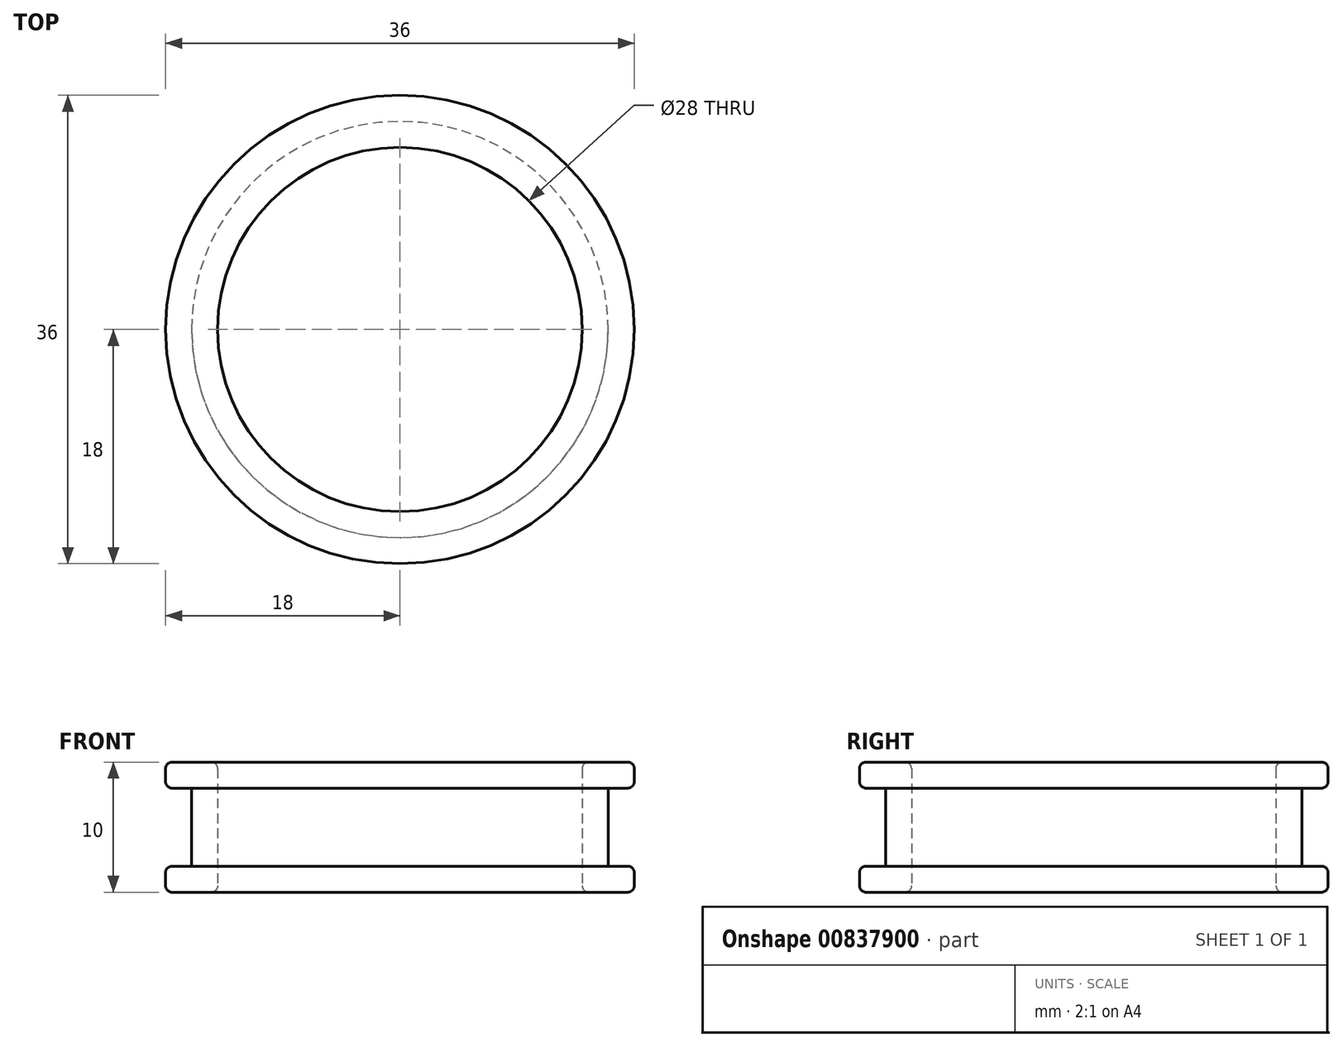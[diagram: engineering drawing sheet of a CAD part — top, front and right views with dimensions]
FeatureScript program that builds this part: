
annotation { "Feature Type Name" : "Feature", "Feature Type Description" : "" }
export const myFeature = defineFeature(function(context is Context, id is Id, definition is map)
    precondition{}
    {
        {
            var Q0;
            Q0=qCreatedBy(makeId("Top.planeOp"),FACE);
            var sketch = newSketch(context, id + "F0", { "sketchPlane" : qUnion([Q0])});
            skCircle(sketch, "E0", {"center": v(0, 0) * mm, "radius": 16 * mm});
            skCircle(sketch, "E1", {"center": v(0, 0) * mm, "radius": 14 * mm});
            skSolve(sketch);
        }
        {
            var Q0;
            Q0=makeQuery(id+"F0.imprint","IMPRINT",FACE,{"disambiguationData":[TD([[makeQuery(id+"F0.imprint","IMPRINT",EDGE,{"derivedFrom":sQuery(id+"F0.wireOp",EDGE,"E0")}),1.0]])]});
            extrude(context, id + "F1", {"entities" : qUnion([Q0]), "depth" : 10 * mm, "offsetDistance" : 25 * mm});
        }
        {
            var Q0;
            Q0=makeQuery(id+"F1.opExtrude","CAP_FACE",FACE,{"disambiguationData":[OSD([sQuery(id+"F0.wireOp",EDGE,"E0"),sQuery(id+"F0.wireOp",EDGE,"E1")])],"isStart":false});
            var sketch = newSketch(context, id + "F2", { "sketchPlane" : qUnion([Q0])});
            skCircle(sketch, "E2", {"center": v(0, 0) * mm, "radius": 18 * mm});
            skSolve(sketch);
        }
        {
            var Q0;
            Q0=makeQuery(id+"F2.imprint","IMPRINT",FACE,{"disambiguationData":[TD([[makeQuery(id+"F2.imprint","IMPRINT",EDGE,{"derivedFrom":sQuery(id+"F2.wireOp",EDGE,"E2")}),1.0]])]});
            extrude(context, id + "F3", {"entities" : qUnion([Q0]), "operationType" : NewBodyOperationType.ADD, "oppositeDirection" : true, "depth" : 2 * mm, "offsetDistance" : 25 * mm});
        }
        {
            var Q0;
            Q0=makeQuery(id+"F1.opExtrude","CAP_FACE",FACE,{"disambiguationData":[OSD([sQuery(id+"F0.wireOp",EDGE,"E0"),sQuery(id+"F0.wireOp",EDGE,"E1")])],"isStart":true});
            var sketch = newSketch(context, id + "F4", { "sketchPlane" : qUnion([Q0])});
            skCircle(sketch, "E3", {"center": v(0, 0) * mm, "radius": 18 * mm});
            skSolve(sketch);
        }
        {
            var Q0;
            Q0=makeQuery(id+"F4.imprint","IMPRINT",FACE,{"disambiguationData":[TD([[makeQuery(id+"F4.imprint","IMPRINT",EDGE,{"derivedFrom":sQuery(id+"F4.wireOp",EDGE,"E3")}),1.0]])]});
            extrude(context, id + "F5", {"entities" : qUnion([Q0]), "operationType" : NewBodyOperationType.ADD, "oppositeDirection" : true, "depth" : 2 * mm, "offsetDistance" : 25 * mm});
        }
        {
            var Q0;
            Q0=makeQuery(id+"F5.opExtrude","CAP_EDGE",EDGE,{"disambiguationData":[OSD([sQuery(id+"F4.wireOp",EDGE,"E3")])],"isStart":true});
            var Q1;
            Q1=makeQuery(id+"F3.opExtrude","CAP_EDGE",EDGE,{"disambiguationData":[OSD([sQuery(id+"F2.wireOp",EDGE,"E2")])],"isStart":true});
            var Q2;
            Q2=makeQuery(id+"F5.opExtrude","CAP_EDGE",EDGE,{"disambiguationData":[OSD([sQuery(id+"F4.wireOp",EDGE,"E3")])],"isStart":false});
            var Q3;
            Q3=makeQuery(id+"F3.opExtrude","CAP_EDGE",EDGE,{"disambiguationData":[OSD([sQuery(id+"F2.wireOp",EDGE,"E2")])],"isStart":false});
            var Q4;
            Q4=makeQuery(id+"F1.opExtrude","CAP_EDGE",EDGE,{"disambiguationData":[OSD([sQuery(id+"F0.wireOp",EDGE,"E1")])],"isStart":true});
            var Q5;
            Q5=makeQuery(id+"F1.opExtrude","CAP_EDGE",EDGE,{"disambiguationData":[OSD([sQuery(id+"F0.wireOp",EDGE,"E1")])],"isStart":false});
            fillet(context, id + "F6", {"entities" : qUnion([Q0, Q1, Q2, Q3, Q4, Q5]), "radius" : .5 * mm, "tangentPropagation" : true, "allowEdgeOverflow" : false});
        }
    });
